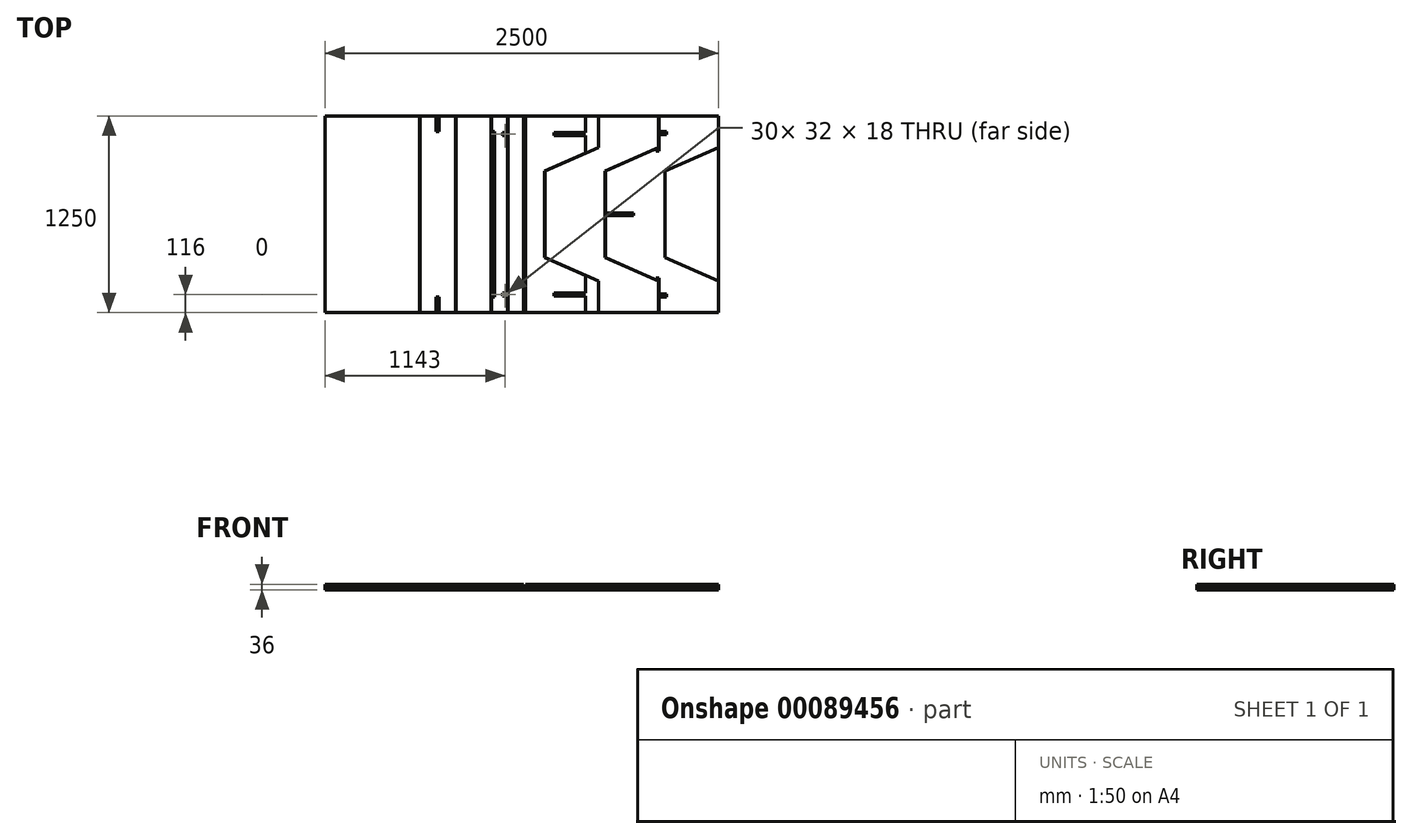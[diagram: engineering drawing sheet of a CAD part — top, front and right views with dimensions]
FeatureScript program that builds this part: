
annotation { "Feature Type Name" : "Feature", "Feature Type Description" : "" }
export const myFeature = defineFeature(function(context is Context, id is Id, definition is map)
    precondition{}
    {
        {
            var Q0;
            Q0=qCreatedBy(makeId("Top.planeOp"),FACE);
            var sketch = newSketch(context, id + "F0", { "sketchPlane" : qUnion([Q0])});
            skLineSegment(sketch, "E0.bottom", {"start": v(0, 0) * mm, "end": v(2500, 0) * mm});
            skLineSegment(sketch, "E0.top", {"start": v(0, 1250) * mm, "end": v(2500, 1250) * mm});
            skLineSegment(sketch, "E0.left", {"start": v(0, 0) * mm, "end": v(0, 1250) * mm});
            skLineSegment(sketch, "E0.right", {"start": v(2500, 0) * mm, "end": v(2500, 1250) * mm});
            skSolve(sketch);
        }
        {
            var Q0;
            Q0 = qSketchRegion(id + "F0", true);
            extrude(context, id + "F1", {"entities" : qUnion([Q0]), "depth" : 18 * mm});
        }
        {
            var Q0;
            Q0=makeQuery(id+"F1.opExtrude","CAP_FACE",FACE,{"disambiguationData":[OSD([sQuery(id+"F0.wireOp",EDGE,"E0.bottom"),sQuery(id+"F0.wireOp",EDGE,"E0.top"),sQuery(id+"F0.wireOp",EDGE,"E0.left"),sQuery(id+"F0.wireOp",EDGE,"E0.right")])],"isStart":false});
            var sketch = newSketch(context, id + "F2", { "sketchPlane" : qUnion([Q0])});
            skLineSegment(sketch, "E1", {"start": v(2500, 1250) * mm, "end": v(2120, 1250) * mm});
            skLineSegment(sketch, "E2", {"start": v(2120, 1250) * mm, "end": v(2120, 1050) * mm});
            skLineSegment(sketch, "E3", {"start": v(2120, 1050) * mm, "end": v(1780, 900) * mm});
            skLineSegment(sketch, "E4", {"start": v(1780, 900) * mm, "end": v(1780, 350) * mm});
            skLineSegment(sketch, "E5", {"start": v(1780, 350) * mm, "end": v(2120, 200) * mm});
            skLineSegment(sketch, "E6", {"start": v(2120, 200) * mm, "end": v(2120, 0) * mm});
            skLineSegment(sketch, "E7", {"start": v(2120, 0) * mm, "end": v(2500, 0) * mm});
            skLineSegment(sketch, "E8", {"start": v(2500, 0) * mm, "end": v(2500, 200) * mm});
            skLineSegment(sketch, "E9", {"start": v(2500, 200) * mm, "end": v(2160, 350) * mm});
            skLineSegment(sketch, "E10", {"start": v(2160, 350) * mm, "end": v(2160, 900) * mm});
            skLineSegment(sketch, "E11", {"start": v(2160, 900) * mm, "end": v(2500, 1050) * mm});
            skLineSegment(sketch, "E12", {"start": v(1780, 625) * mm, "end": v(2500, 625) * mm, "construction": true});
            skLineSegment(sketch, "E13", {"start": v(2500, 1250) * mm, "end": v(2500, 1050) * mm});
            skLineSegment(sketch, "E14", {"start": v(2500, 200) * mm, "end": v(2500, 0) * mm});
            skSolve(sketch);
        }
        {
            var Q0;
            Q0=makeQuery(id+"F2.imprint","IMPRINT",FACE,{"disambiguationData":[TD([[makeQuery(id+"F2.imprint","IMPRINT",EDGE,{"derivedFrom":sQuery(id+"F2.wireOp",EDGE,"E1")}),-1.0]])]});
            extrude(context, id + "F3", {"entities" : qUnion([Q0]), "depth" : 18 * mm});
        }
        {
            var Q0;
            Q0=makeQuery(id+"F3.opExtrude","SWEPT_BODY",BODY,{"disambiguationData":[OSD([sQuery(id+"F2.wireOp",EDGE,"E1"),sQuery(id+"F2.wireOp",EDGE,"E2"),sQuery(id+"F2.wireOp",EDGE,"E3"),sQuery(id+"F2.wireOp",EDGE,"E4"),sQuery(id+"F2.wireOp",EDGE,"E5"),sQuery(id+"F2.wireOp",EDGE,"E6"),sQuery(id+"F2.wireOp",EDGE,"E7"),sQuery(id+"F2.wireOp",EDGE,"E9"),sQuery(id+"F2.wireOp",EDGE,"E10"),sQuery(id+"F2.wireOp",EDGE,"E11"),sQuery(id+"F2.wireOp",EDGE,"E13"),sQuery(id+"F2.wireOp",EDGE,"E14")])]});
            transform(context, id + "F4", {"entities" : qUnion([Q0]), "transformType" : TransformType.TRANSLATION_3D, "dx" : -383 * mm, "dy" : 0 * mm, "dz" : 0 * mm, "makeCopy" : true});
        }
        {
            var Q0;
            Q0=makeQuery(id+"F1.opExtrude","CAP_FACE",FACE,{"disambiguationData":[OSD([sQuery(id+"F0.wireOp",EDGE,"E0.bottom"),sQuery(id+"F0.wireOp",EDGE,"E0.top"),sQuery(id+"F0.wireOp",EDGE,"E0.left"),sQuery(id+"F0.wireOp",EDGE,"E0.right")])],"isStart":false});
            var sketch = newSketch(context, id + "F5", { "sketchPlane" : qUnion([Q0])});
            skLineSegment(sketch, "E15", {"start": v(1734, 1250) * mm, "end": v(1734, 1050) * mm});
            skLineSegment(sketch, "E16", {"start": v(1734, 1050) * mm, "end": v(1394, 900) * mm});
            skLineSegment(sketch, "E17", {"start": v(1394, 900) * mm, "end": v(1394, 350) * mm});
            skLineSegment(sketch, "E18", {"start": v(1394, 350) * mm, "end": v(1734, 200) * mm});
            skLineSegment(sketch, "E19", {"start": v(1734, 200) * mm, "end": v(1734, 0) * mm});
            skLineSegment(sketch, "E20", {"start": v(1734, 0) * mm, "end": v(1274, 0) * mm});
            skLineSegment(sketch, "E21", {"start": v(1274, 0) * mm, "end": v(1274, 1250) * mm});
            skLineSegment(sketch, "E22", {"start": v(1274, 1250) * mm, "end": v(1734, 1250) * mm});
            skLineSegment(sketch, "E23", {"start": v(1274, 625) * mm, "end": v(1394, 625) * mm, "construction": true});
            skLineSegment(sketch, "E24", {"start": v(1654, 1250) * mm, "end": v(1654, 1014.7) * mm});
            skLineSegment(sketch, "E25", {"start": v(1654, 235.3) * mm, "end": v(1654, 0) * mm});
            skLineSegment(sketch, "E26", {"start": v(1654, 1014.7) * mm, "end": v(1654, 235.3) * mm, "construction": true});
            skSolve(sketch);
        }
        {
            var Q0;
            {var subQ3=sQuery(id+"F5.wireOp",EDGE,"E17");Q0=makeQuery(id+"F5.imprint","IMPRINT",FACE,{"disambiguationData":[TD([[makeQuery(id+"F5.imprint","IMPRINT",EDGE,{"derivedFrom":subQ3}),-1.0]])]});}
            extrude(context, id + "F6", {"entities" : qUnion([Q0]), "depth" : 18 * mm});
        }
        {
            var Q0;
            Q0=makeQuery(id+"F1.opExtrude","CAP_FACE",FACE,{"disambiguationData":[OSD([sQuery(id+"F0.wireOp",EDGE,"E0.bottom"),sQuery(id+"F0.wireOp",EDGE,"E0.top"),sQuery(id+"F0.wireOp",EDGE,"E0.left"),sQuery(id+"F0.wireOp",EDGE,"E0.right")])],"isStart":false});
            var sketch = newSketch(context, id + "F7", { "sketchPlane" : qUnion([Q0])});
            skLineSegment(sketch, "E27.bottom", {"start": v(0, 1250) * mm, "end": v(600, 1250) * mm});
            skLineSegment(sketch, "E27.top", {"start": v(0, 0) * mm, "end": v(600, 0) * mm});
            skLineSegment(sketch, "E27.left", {"start": v(0, 1250) * mm, "end": v(0, 0) * mm});
            skLineSegment(sketch, "E27.right", {"start": v(600, 1250) * mm, "end": v(600, 0) * mm});
            skSolve(sketch);
        }
        {
            var Q0;
            Q0 = qSketchRegion(id + "F7", true);
            extrude(context, id + "F8", {"entities" : qUnion([Q0]), "depth" : 18 * mm});
        }
        {
            var Q0;
            Q0=makeQuery(id+"F1.opExtrude","CAP_FACE",FACE,{"disambiguationData":[OSD([sQuery(id+"F0.wireOp",EDGE,"E0.bottom"),sQuery(id+"F0.wireOp",EDGE,"E0.top"),sQuery(id+"F0.wireOp",EDGE,"E0.left"),sQuery(id+"F0.wireOp",EDGE,"E0.right")])],"isStart":false});
            var sketch = newSketch(context, id + "F9", { "sketchPlane" : qUnion([Q0])});
            skLineSegment(sketch, "E28.bottom", {"start": v(603, 1250) * mm, "end": v(828, 1250) * mm});
            skLineSegment(sketch, "E28.top", {"start": v(603, 0) * mm, "end": v(828, 0) * mm});
            skLineSegment(sketch, "E28.left", {"start": v(603, 1250) * mm, "end": v(603, 0) * mm});
            skLineSegment(sketch, "E28.right", {"start": v(828, 1250) * mm, "end": v(828, 0) * mm});
            skSolve(sketch);
        }
        {
            var Q0;
            Q0 = qSketchRegion(id + "F9", true);
            extrude(context, id + "F10", {"entities" : qUnion([Q0]), "depth" : 18 * mm});
        }
        {
            var Q0;
            Q0=makeQuery(id+"F10.opExtrude","SWEPT_BODY",BODY,{"disambiguationData":[OSD([sQuery(id+"F9.wireOp",EDGE,"E28.bottom"),sQuery(id+"F9.wireOp",EDGE,"E28.top"),sQuery(id+"F9.wireOp",EDGE,"E28.left"),sQuery(id+"F9.wireOp",EDGE,"E28.right")])]});
            transform(context, id + "F11", {"entities" : qUnion([Q0]), "transformType" : TransformType.TRANSLATION_3D, "dx" : (250 + 3 - 25) * mm, "dy" : 0 * mm, "dz" : 0 * mm, "makeCopy" : true});
        }
        {
            var Q0;
            Q0=makeQuery(id+"F1.opExtrude","CAP_FACE",FACE,{"disambiguationData":[OSD([sQuery(id+"F0.wireOp",EDGE,"E0.bottom"),sQuery(id+"F0.wireOp",EDGE,"E0.top"),sQuery(id+"F0.wireOp",EDGE,"E0.left"),sQuery(id+"F0.wireOp",EDGE,"E0.right")])],"isStart":false});
            var sketch = newSketch(context, id + "F12", { "sketchPlane" : qUnion([Q0])});
            skLineSegment(sketch, "E29.bottom", {"start": v(1059, 1250) * mm, "end": v(1159, 1250) * mm});
            skLineSegment(sketch, "E29.top", {"start": v(1059, 0) * mm, "end": v(1159, 0) * mm});
            skLineSegment(sketch, "E29.left", {"start": v(1059, 1250) * mm, "end": v(1059, 0) * mm});
            skLineSegment(sketch, "E29.right", {"start": v(1159, 1250) * mm, "end": v(1159, 0) * mm});
            skSolve(sketch);
        }
        {
            var Q0;
            Q0 = qSketchRegion(id + "F12", true);
            extrude(context, id + "F13", {"entities" : qUnion([Q0]), "depth" : 18 * mm});
        }
        {
            var Q0;
            Q0=makeQuery(id+"F13.opExtrude","SWEPT_BODY",BODY,{"disambiguationData":[OSD([sQuery(id+"F12.wireOp",EDGE,"E29.bottom"),sQuery(id+"F12.wireOp",EDGE,"E29.top"),sQuery(id+"F12.wireOp",EDGE,"E29.left"),sQuery(id+"F12.wireOp",EDGE,"E29.right")])]});
            transform(context, id + "F14", {"entities" : qUnion([Q0]), "transformType" : TransformType.TRANSLATION_3D, "dx" : 103 * mm, "dy" : 0 * mm, "dz" : 0 * mm, "makeCopy" : true});
        }
        {
            var Q0;
            Q0=makeQuery(id+"F13.opExtrude","CAP_FACE",FACE,{"disambiguationData":[OSD([sQuery(id+"F12.wireOp",EDGE,"E29.bottom"),sQuery(id+"F12.wireOp",EDGE,"E29.top"),sQuery(id+"F12.wireOp",EDGE,"E29.left"),sQuery(id+"F12.wireOp",EDGE,"E29.right")])],"isStart":false});
            var sketch = newSketch(context, id + "F15", { "sketchPlane" : qUnion([Q0])});
            skLineSegment(sketch, "E30.bottom", {"start": v(1059, 1150) * mm, "end": v(1077, 1150) * mm});
            skLineSegment(sketch, "E30.top", {"start": v(1059, 100) * mm, "end": v(1077, 100) * mm});
            skLineSegment(sketch, "E30.left", {"start": v(1059, 1150) * mm, "end": v(1059, 100) * mm});
            skLineSegment(sketch, "E30.right", {"start": v(1077, 1150) * mm, "end": v(1077, 100) * mm});
            skLineSegment(sketch, "E31", {"start": v(1077, 625) * mm, "end": v(1159, 625) * mm});
            skSolve(sketch);
        }
        {
            var Q0;
            Q0 = qSketchRegion(id + "F15", true);
            extrude(context, id + "F16", {"entities" : qUnion([Q0]), "operationType" : NewBodyOperationType.REMOVE, "oppositeDirection" : true, "depth" : 18 * mm});
        }
        {
            var Q0;
            Q0=makeQuery(id+"F13.opExtrude","CAP_FACE",FACE,{"disambiguationData":[OSD([sQuery(id+"F12.wireOp",EDGE,"E29.bottom"),sQuery(id+"F12.wireOp",EDGE,"E29.top"),sQuery(id+"F12.wireOp",EDGE,"E29.left"),sQuery(id+"F12.wireOp",EDGE,"E29.right")])],"isStart":false});
            var sketch = newSketch(context, id + "F17", { "sketchPlane" : qUnion([Q0])});
            skLineSegment(sketch, "E32.bottom", {"start": v(1159, 107) * mm, "end": v(1127, 107) * mm});
            skLineSegment(sketch, "E32.top", {"start": v(1159, 125) * mm, "end": v(1127, 125) * mm});
            skLineSegment(sketch, "E32.left", {"start": v(1159, 125) * mm, "end": v(1159, 107) * mm});
            skLineSegment(sketch, "E32.right", {"start": v(1127, 125) * mm, "end": v(1127, 107) * mm});
            skLineSegment(sketch, "E33.bottom", {"start": v(1159, 1143) * mm, "end": v(1127, 1143) * mm});
            skLineSegment(sketch, "E33.top", {"start": v(1159, 1125) * mm, "end": v(1127, 1125) * mm});
            skLineSegment(sketch, "E33.left", {"start": v(1159, 1143) * mm, "end": v(1159, 1125) * mm});
            skLineSegment(sketch, "E33.right", {"start": v(1127, 1143) * mm, "end": v(1127, 1125) * mm});
            skLineSegment(sketch, "E34", {"start": v(1127, 107) * mm, "end": v(1127, 0) * mm, "construction": true});
            skLineSegment(sketch, "E35", {"start": v(1127, 1143) * mm, "end": v(1127, 1250) * mm});
            skSolve(sketch);
        }
        {
            var Q0;
            Q0 = qSketchRegion(id + "F17", true);
            extrude(context, id + "F18", {"entities" : qUnion([Q0]), "operationType" : NewBodyOperationType.REMOVE, "endBound" : BoundingType.THROUGH_ALL, "oppositeDirection" : true, "depth" : 25 * mm});
        }
        {
            var Q0;
            Q0=makeQuery(id+"F11.opPattern","COPY",FACE,{"derivedFrom":makeQuery(id+"F10.opExtrude","CAP_FACE",FACE,{"disambiguationData":[OSD([sQuery(id+"F9.wireOp",EDGE,"E28.bottom"),sQuery(id+"F9.wireOp",EDGE,"E28.top"),sQuery(id+"F9.wireOp",EDGE,"E28.left"),sQuery(id+"F9.wireOp",EDGE,"E28.right")])],"isStart":false}),"instanceName":"1"});
            var sketch = newSketch(context, id + "F19", { "sketchPlane" : qUnion([Q0])});
            skLineSegment(sketch, "E36.bottom", {"start": v(706.5, 1250) * mm, "end": v(724.5, 1250) * mm});
            skLineSegment(sketch, "E36.top", {"start": v(706.5, 1150) * mm, "end": v(724.5, 1150) * mm});
            skLineSegment(sketch, "E36.left", {"start": v(706.5, 1250) * mm, "end": v(706.5, 1150) * mm});
            skLineSegment(sketch, "E36.right", {"start": v(724.5, 1250) * mm, "end": v(724.5, 1150) * mm});
            skLineSegment(sketch, "E37.bottom", {"start": v(706.5, 100) * mm, "end": v(724.5, 100) * mm});
            skLineSegment(sketch, "E37.top", {"start": v(706.5, 0) * mm, "end": v(724.5, 0) * mm});
            skLineSegment(sketch, "E37.left", {"start": v(706.5, 100) * mm, "end": v(706.5, 0) * mm});
            skLineSegment(sketch, "E37.right", {"start": v(724.5, 100) * mm, "end": v(724.5, 0) * mm});
            skLineSegment(sketch, "E38", {"start": v(715.5, 100) * mm, "end": v(715.5, 1150) * mm, "construction": true});
            skLineSegment(sketch, "E39", {"start": v(724.5, 1150) * mm, "end": v(828, 1150) * mm, "construction": true});
            skLineSegment(sketch, "E40", {"start": v(706.5, 1150) * mm, "end": v(603, 1150) * mm, "construction": true});
            skSolve(sketch);
        }
        {
            var Q0;
            Q0 = qSketchRegion(id + "F19", true);
            extrude(context, id + "F20", {"entities" : qUnion([Q0]), "operationType" : NewBodyOperationType.REMOVE, "oppositeDirection" : true, "depth" : 18 * mm});
        }
        {
            var Q0;
            Q0=makeQuery(id+"F3.opExtrude","CAP_FACE",FACE,{"disambiguationData":[OSD([sQuery(id+"F2.wireOp",EDGE,"E1"),sQuery(id+"F2.wireOp",EDGE,"E2"),sQuery(id+"F2.wireOp",EDGE,"E3"),sQuery(id+"F2.wireOp",EDGE,"E4"),sQuery(id+"F2.wireOp",EDGE,"E5"),sQuery(id+"F2.wireOp",EDGE,"E6"),sQuery(id+"F2.wireOp",EDGE,"E7"),sQuery(id+"F2.wireOp",EDGE,"E9"),sQuery(id+"F2.wireOp",EDGE,"E10"),sQuery(id+"F2.wireOp",EDGE,"E11"),sQuery(id+"F2.wireOp",EDGE,"E13"),sQuery(id+"F2.wireOp",EDGE,"E14")])],"isStart":false});
            var sketch = newSketch(context, id + "F21", { "sketchPlane" : qUnion([Q0])});
            skLineSegment(sketch, "E41.bottom", {"start": v(2120, 118) * mm, "end": v(2170, 118) * mm});
            skLineSegment(sketch, "E41.top", {"start": v(2120, 100) * mm, "end": v(2170, 100) * mm});
            skLineSegment(sketch, "E41.left", {"start": v(2120, 118) * mm, "end": v(2120, 100) * mm});
            skLineSegment(sketch, "E41.right", {"start": v(2170, 118) * mm, "end": v(2170, 100) * mm});
            skLineSegment(sketch, "E42.bottom", {"start": v(2120, 1150) * mm, "end": v(2170, 1150) * mm});
            skLineSegment(sketch, "E42.top", {"start": v(2120, 1132) * mm, "end": v(2170, 1132) * mm});
            skLineSegment(sketch, "E42.left", {"start": v(2120, 1150) * mm, "end": v(2120, 1132) * mm});
            skLineSegment(sketch, "E42.right", {"start": v(2170, 1150) * mm, "end": v(2170, 1132) * mm});
            skLineSegment(sketch, "E43", {"start": v(2120, 200) * mm, "end": v(2120, 221.5) * mm});
            skLineSegment(sketch, "E44", {"start": v(2120, 221.5) * mm, "end": v(2102, 221.5) * mm});
            skLineSegment(sketch, "E45", {"start": v(2102, 221.5) * mm, "end": v(2102, 207.94) * mm});
            skLineSegment(sketch, "E46", {"start": v(2120, 1050) * mm, "end": v(2120, 1028.5) * mm});
            skLineSegment(sketch, "E47", {"start": v(2120, 1028.5) * mm, "end": v(2102, 1028.5) * mm});
            skLineSegment(sketch, "E48", {"start": v(2102, 1028.5) * mm, "end": v(2102, 1042.06) * mm});
            skSolve(sketch);
        }
        {
            var Q0;
            Q0 = qSketchRegion(id + "F21", true);
            var Q1;
            {var subQ0=sQuery(id+"F21.wireOp",EDGE,"E46");Q1=makeQuery(id+"F21.imprint","IMPRINT",FACE,{"disambiguationData":[TD([[makeQuery(id+"F21.imprint","IMPRINT",EDGE,{"derivedFrom":subQ0}),-1.0]])]});}
            var Q2;
            {var subQ0=sQuery(id+"F21.wireOp",EDGE,"E43");Q2=makeQuery(id+"F21.imprint","IMPRINT",FACE,{"disambiguationData":[TD([[makeQuery(id+"F21.imprint","IMPRINT",EDGE,{"derivedFrom":subQ0}),1.0]])]});}
            extrude(context, id + "F22", {"entities" : qUnion([Q0, Q1, Q2]), "operationType" : NewBodyOperationType.REMOVE, "endBound" : BoundingType.UP_TO_NEXT, "oppositeDirection" : true, "depth" : 25 * mm});
        }
        {
            var Q0;
            Q0=makeQuery(id+"F3.opExtrude","CAP_FACE",FACE,{"disambiguationData":[OSD([sQuery(id+"F2.wireOp",EDGE,"E1"),sQuery(id+"F2.wireOp",EDGE,"E2"),sQuery(id+"F2.wireOp",EDGE,"E3"),sQuery(id+"F2.wireOp",EDGE,"E4"),sQuery(id+"F2.wireOp",EDGE,"E5"),sQuery(id+"F2.wireOp",EDGE,"E6"),sQuery(id+"F2.wireOp",EDGE,"E7"),sQuery(id+"F2.wireOp",EDGE,"E9"),sQuery(id+"F2.wireOp",EDGE,"E10"),sQuery(id+"F2.wireOp",EDGE,"E11"),sQuery(id+"F2.wireOp",EDGE,"E13"),sQuery(id+"F2.wireOp",EDGE,"E14")])],"isStart":false});
            var sketch = newSketch(context, id + "F23", { "sketchPlane" : qUnion([Q0])});
            skLineSegment(sketch, "E49.bottom", {"start": v(1780, 634) * mm, "end": v(1960, 634) * mm});
            skLineSegment(sketch, "E49.top", {"start": v(1780, 616) * mm, "end": v(1960, 616) * mm});
            skLineSegment(sketch, "E49.left", {"start": v(1780, 634) * mm, "end": v(1780, 616) * mm});
            skLineSegment(sketch, "E49.right", {"start": v(1960, 634) * mm, "end": v(1960, 616) * mm});
            skPoint(sketch, "E50", {"position": v(1780, 625) * mm});
            skSolve(sketch);
        }
        {
            var Q0;
            Q0 = qSketchRegion(id + "F23", true);
            extrude(context, id + "F24", {"entities" : qUnion([Q0]), "operationType" : NewBodyOperationType.REMOVE, "endBound" : BoundingType.UP_TO_NEXT, "oppositeDirection" : true, "depth" : 25 * mm});
        }
        {
            var Q0;
            Q0=makeQuery(id+"F6.opExtrude","CAP_FACE",FACE,{"disambiguationData":[OSD([sQuery(id+"F5.wireOp",EDGE,"E16"),sQuery(id+"F5.wireOp",EDGE,"E17"),sQuery(id+"F5.wireOp",EDGE,"E18"),sQuery(id+"F5.wireOp",EDGE,"E20"),sQuery(id+"F5.wireOp",EDGE,"E21"),sQuery(id+"F5.wireOp",EDGE,"E22"),sQuery(id+"F5.wireOp",EDGE,"E24"),sQuery(id+"F5.wireOp",EDGE,"E25")])],"isStart":false});
            var sketch = newSketch(context, id + "F25", { "sketchPlane" : qUnion([Q0])});
            skLineSegment(sketch, "E51.bottom", {"start": v(1654, 1143) * mm, "end": v(1454, 1143) * mm});
            skLineSegment(sketch, "E51.top", {"start": v(1654, 1125) * mm, "end": v(1454, 1125) * mm});
            skLineSegment(sketch, "E51.left", {"start": v(1654, 1143) * mm, "end": v(1654, 1125) * mm});
            skLineSegment(sketch, "E51.right", {"start": v(1454, 1143) * mm, "end": v(1454, 1125) * mm});
            skLineSegment(sketch, "E52.bottom", {"start": v(1654, 125) * mm, "end": v(1454, 125) * mm});
            skLineSegment(sketch, "E52.top", {"start": v(1654, 107) * mm, "end": v(1454, 107) * mm});
            skLineSegment(sketch, "E52.left", {"start": v(1654, 125) * mm, "end": v(1654, 107) * mm});
            skLineSegment(sketch, "E52.right", {"start": v(1454, 125) * mm, "end": v(1454, 107) * mm});
            skLineSegment(sketch, "E53", {"start": v(1454, 1143) * mm, "end": v(1454, 1250) * mm, "construction": true});
            skLineSegment(sketch, "E54", {"start": v(1454, 107) * mm, "end": v(1454, 0) * mm, "construction": true});
            skSolve(sketch);
        }
        {
            var Q0;
            Q0 = qSketchRegion(id + "F25", true);
            extrude(context, id + "F26", {"entities" : qUnion([Q0]), "operationType" : NewBodyOperationType.REMOVE, "endBound" : BoundingType.UP_TO_NEXT, "oppositeDirection" : true, "depth" : 25 * mm});
        }
    });
